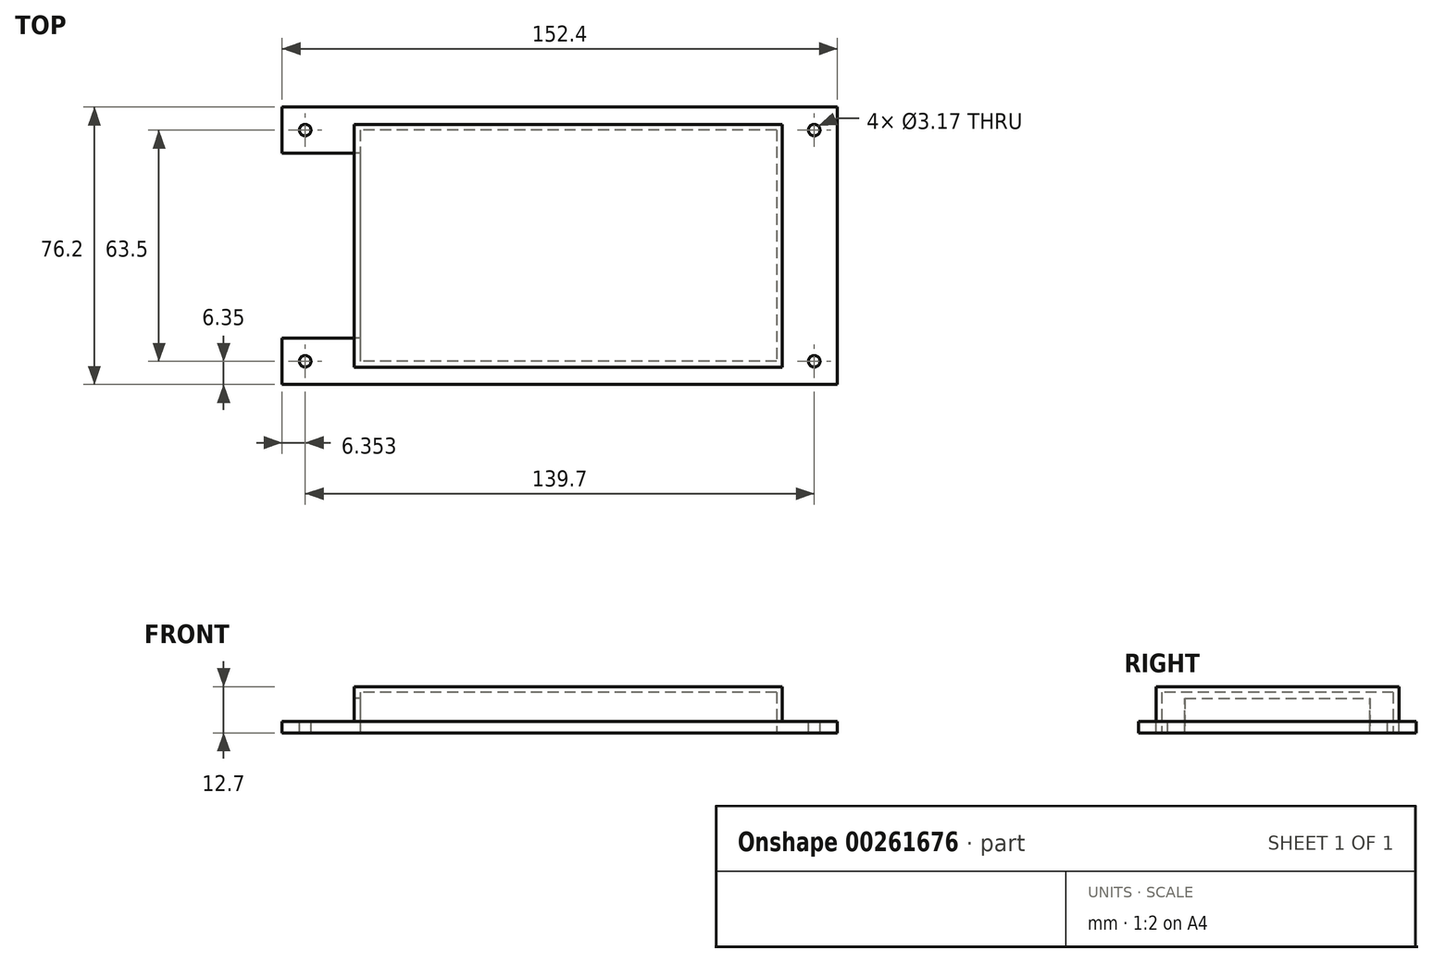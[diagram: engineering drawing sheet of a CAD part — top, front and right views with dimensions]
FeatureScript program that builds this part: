
annotation { "Feature Type Name" : "Feature", "Feature Type Description" : "" }
export const myFeature = defineFeature(function(context is Context, id is Id, definition is map)
    precondition{}
    {
        {
            var Q0;
            Q0=qCreatedBy(makeId("Top.planeOp"),FACE);
            var sketch = newSketch(context, id + "F0", { "sketchPlane" : qUnion([Q0])});
            skLineSegment(sketch, "E0.bottom", {"start": v(73.83, -38.1) * mm, "end": v(-78.57, -38.1) * mm});
            skLineSegment(sketch, "E0.top", {"start": v(73.83, 38.1) * mm, "end": v(-78.57, 38.1) * mm});
            skLineSegment(sketch, "E0.left", {"start": v(73.83, -38.1) * mm, "end": v(73.83, 38.1) * mm});
            skLineSegment(sketch, "E0.right", {"start": v(-78.57, -38.1) * mm, "end": v(-78.57, 38.1) * mm});
            skPoint(sketch, "E0.middle", {"position": v(-2.37, 0) * mm});
            skSolve(sketch);
        }
        {
            var Q0;
            Q0 = qSketchRegion(id + "F0", true);
            extrude(context, id + "F1", {"entities" : qUnion([Q0]), "depth" : 3.17 * mm});
        }
        {
            var Q0;
            Q0=makeQuery(id+"F1.opExtrude","CAP_FACE",FACE,{"disambiguationData":[OSD([sQuery(id+"F0.wireOp",EDGE,"E0.bottom"),sQuery(id+"F0.wireOp",EDGE,"E0.top"),sQuery(id+"F0.wireOp",EDGE,"E0.left"),sQuery(id+"F0.wireOp",EDGE,"E0.right")])],"isStart":false});
            var sketch = newSketch(context, id + "F2", { "sketchPlane" : qUnion([Q0])});
            skLineSegment(sketch, "E1.bottom", {"start": v(58.74, -33.34) * mm, "end": v(-58.74, -33.34) * mm});
            skLineSegment(sketch, "E1.top", {"start": v(58.74, 33.34) * mm, "end": v(-58.74, 33.34) * mm});
            skLineSegment(sketch, "E1.left", {"start": v(58.74, -33.34) * mm, "end": v(58.74, 33.34) * mm});
            skLineSegment(sketch, "E1.right", {"start": v(-58.74, -33.34) * mm, "end": v(-58.74, 33.34) * mm});
            skPoint(sketch, "E1.middle", {"position": v(0, 0) * mm});
            skSolve(sketch);
        }
        {
            var Q0;
            Q0 = qSketchRegion(id + "F2", true);
            extrude(context, id + "F3", {"entities" : qUnion([Q0]), "operationType" : NewBodyOperationType.ADD, "depth" : 9.52 * mm});
        }
        {
            var Q0;
            Q0=makeQuery(id+"F1.opExtrude","CAP_FACE",FACE,{"disambiguationData":[OSD([sQuery(id+"F0.wireOp",EDGE,"E0.bottom"),sQuery(id+"F0.wireOp",EDGE,"E0.top"),sQuery(id+"F0.wireOp",EDGE,"E0.left"),sQuery(id+"F0.wireOp",EDGE,"E0.right")])],"isStart":true});
            var sketch = newSketch(context, id + "F4", { "sketchPlane" : qUnion([Q0])});
            skLineSegment(sketch, "E2.bottom", {"start": v(57.15, -31.75) * mm, "end": v(-57.15, -31.75) * mm});
            skLineSegment(sketch, "E2.top", {"start": v(57.15, 31.75) * mm, "end": v(-57.15, 31.75) * mm});
            skLineSegment(sketch, "E2.left", {"start": v(57.15, -31.75) * mm, "end": v(57.15, 31.75) * mm});
            skLineSegment(sketch, "E2.right", {"start": v(-57.15, -31.75) * mm, "end": v(-57.15, 31.75) * mm});
            skPoint(sketch, "E2.middle", {"position": v(0, 0) * mm});
            skSolve(sketch);
        }
        {
            var Q0;
            Q0 = qSketchRegion(id + "F4", true);
            extrude(context, id + "F5", {"entities" : qUnion([Q0]), "operationType" : NewBodyOperationType.REMOVE, "oppositeDirection" : true, "depth" : 11.1 * mm});
        }
        {
            var Q0;
            Q0=makeQuery(id+"F3.opExtrude","SWEPT_FACE",FACE,{"disambiguationData":[OSD([sQuery(id+"F2.wireOp",EDGE,"E1.right")])]});
            var sketch = newSketch(context, id + "F6", { "sketchPlane" : qUnion([Q0])});
            skLineSegment(sketch, "E3.bottom", {"start": v(25.4, 0) * mm, "end": v(-25.4, 0) * mm});
            skLineSegment(sketch, "E3.top", {"start": v(25.4, 9.52) * mm, "end": v(-25.4, 9.53) * mm});
            skLineSegment(sketch, "E3.left", {"start": v(25.4, 0) * mm, "end": v(25.4, 9.53) * mm});
            skLineSegment(sketch, "E3.right", {"start": v(-25.4, 0) * mm, "end": v(-25.4, 9.53) * mm});
            skPoint(sketch, "E3.middle", {"position": v(0, 4.76) * mm});
            skPoint(sketch, "E4", {"position": v(0, 12.7) * mm});
            skSolve(sketch);
        }
        {
            var Q0;
            Q0 = qSketchRegion(id + "F6", true);
            extrude(context, id + "F7", {"entities" : qUnion([Q0]), "operationType" : NewBodyOperationType.REMOVE, "oppositeDirection" : true, "depth" : 25.4 * mm, "hasSecondDirection" : true, "secondDirectionOppositeDirection" : false, "secondDirectionDepth" : 25.4 * mm});
        }
        {
            var Q0;
            Q0=makeQuery(id+"F1.opExtrude","CAP_FACE",FACE,{"disambiguationData":[OSD([sQuery(id+"F0.wireOp",EDGE,"E0.bottom"),sQuery(id+"F0.wireOp",EDGE,"E0.top"),sQuery(id+"F0.wireOp",EDGE,"E0.left"),sQuery(id+"F0.wireOp",EDGE,"E0.right")])],"isStart":false});
            var sketch = newSketch(context, id + "F8", { "sketchPlane" : qUnion([Q0])});
            skCircle(sketch, "E5", {"center": v(-72.22, 31.75) * mm, "radius": 1.59 * mm});
            skCircle(sketch, "E6", {"center": v(-72.22, -31.75) * mm, "radius": 1.59 * mm});
            skCircle(sketch, "E7", {"center": v(67.48, 31.75) * mm, "radius": 1.59 * mm});
            skCircle(sketch, "E8", {"center": v(67.48, -31.75) * mm, "radius": 1.59 * mm});
            skSolve(sketch);
        }
        {
            var Q0;
            Q0 = qSketchRegion(id + "F8", true);
            extrude(context, id + "F9", {"entities" : qUnion([Q0]), "operationType" : NewBodyOperationType.REMOVE, "oppositeDirection" : true, "depth" : 25.4 * mm});
        }
    });
